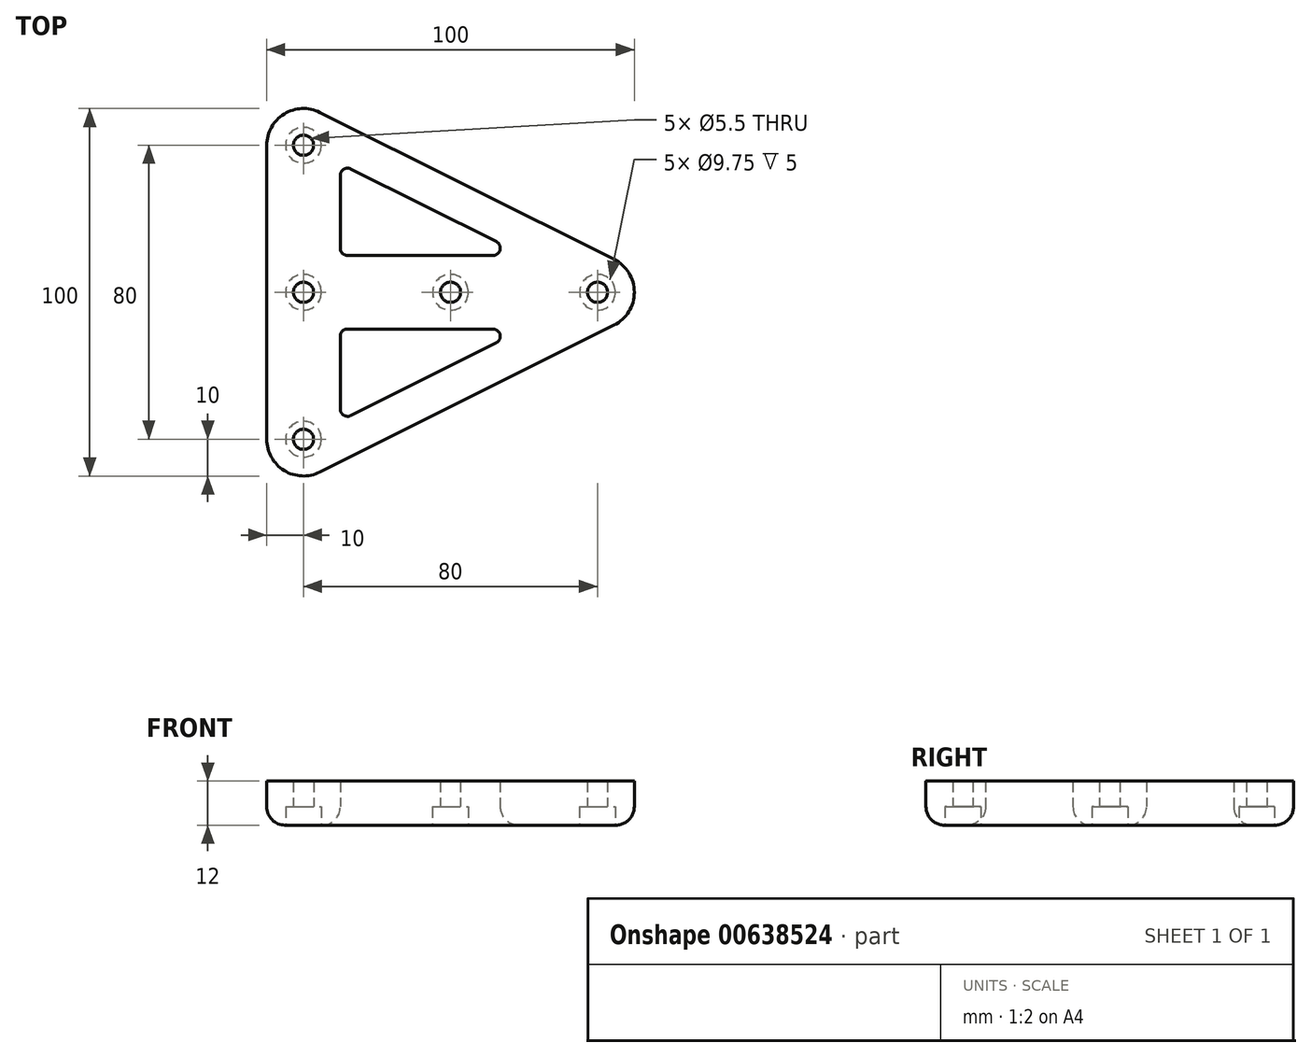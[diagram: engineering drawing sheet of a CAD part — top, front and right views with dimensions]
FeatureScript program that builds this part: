
annotation { "Feature Type Name" : "Feature", "Feature Type Description" : "" }
export const myFeature = defineFeature(function(context is Context, id is Id, definition is map)
    precondition{}
    {
        {
            var Q0;
            Q0=qCreatedBy(makeId("Top.planeOp"),FACE);
            var sketch = newSketch(context, id + "F0", { "sketchPlane" : qUnion([Q0])});
            skArc(sketch, "E0", {"start": v(4.47, 48.94) * mm, "mid": v(-5.26, 48.5) * mm, "end": v(-10, 40) * mm});
            skArc(sketch, "E1.MirrorC", {"start": v(4.47, -48.94) * mm, "mid": v(-5.26, -48.5) * mm, "end": v(-10, -40) * mm});
            skArc(sketch, "E2", {"start": v(84.47, -8.94) * mm, "mid": v(90, 0) * mm, "end": v(84.47, 8.94) * mm});
            skLineSegment(sketch, "E3", {"start": v(4.47, 48.94) * mm, "end": v(84.47, 8.94) * mm});
            skLineSegment(sketch, "E4", {"start": v(4.47, -48.94) * mm, "end": v(84.47, -8.94) * mm});
            skLineSegment(sketch, "E5", {"start": v(-10, 40) * mm, "end": v(-10, -40) * mm});
            skPoint(sketch, "E6", {"position": v(0, 0) * mm});
            skPoint(sketch, "E7", {"position": v(40, 0) * mm});
            skLineSegment(sketch, "E8.0", {"start": v(12.9, 33.55) * mm, "end": v(52.42, 13.79) * mm});
            skLineSegment(sketch, "E9.0", {"start": v(10, 31.76) * mm, "end": v(10, 12) * mm});
            skLineSegment(sketch, "E10.0", {"start": v(12, 10) * mm, "end": v(51.53, 10) * mm});
            skPoint(sketch, "E11.visualSharp", {"position": v(10, 35) * mm});
            skArc(sketch, "E11.filletArc", {"start": v(12.9, 33.55) * mm, "mid": v(10.95, 33.47) * mm, "end": v(10, 31.76) * mm});
            skPoint(sketch, "E12.visualSharp", {"position": v(10, 10) * mm});
            skArc(sketch, "E12.filletArc", {"start": v(10, 12) * mm, "mid": v(10.59, 10.59) * mm, "end": v(12, 10) * mm});
            skPoint(sketch, "E13.visualSharp", {"position": v(60, 10) * mm});
            skArc(sketch, "E13.filletArc", {"start": v(51.53, 10) * mm, "mid": v(53.47, 11.54) * mm, "end": v(52.42, 13.79) * mm});
            skArc(sketch, "E14.MirrorCS", {"start": v(10, -12) * mm, "mid": v(10.59, -10.59) * mm, "end": v(12, -10) * mm});
            skArc(sketch, "E15.MirrorCS", {"start": v(51.53, -10) * mm, "mid": v(53.47, -11.54) * mm, "end": v(52.42, -13.79) * mm});
            skPoint(sketch, "E16.MirrorP", {"position": v(10, -10) * mm});
            skArc(sketch, "E17.MirrorCS", {"start": v(12.9, -33.55) * mm, "mid": v(10.95, -33.47) * mm, "end": v(10, -31.76) * mm});
            skLineSegment(sketch, "E18.MirrorCS", {"start": v(10, -31.76) * mm, "end": v(10, -12) * mm});
            skLineSegment(sketch, "E19.MirrorCS", {"start": v(12, -10) * mm, "end": v(51.53, -10) * mm});
            skLineSegment(sketch, "E20.MirrorCS", {"start": v(12.9, -33.55) * mm, "end": v(52.42, -13.79) * mm});
            skSolve(sketch);
        }
        {
            var Q0;
            Q0=makeQuery(id+"F0.imprint","IMPRINT",FACE,{"disambiguationData":[TD([[makeQuery(id+"F0.imprint","IMPRINT",EDGE,{"derivedFrom":sQuery(id+"F0.wireOp",EDGE,"E0")}),1.0]])]});
            extrude(context, id + "F1", {"entities" : qUnion([Q0]), "depth" : 12 * mm, "offsetDistance" : 25 * mm});
        }
        {
            var Q0;
            Q0=sQuery(id+"F0.wireOp",VERTEX,"E0.center");
            var Q1;
            Q1=sQuery(id+"F0.wireOp",VERTEX,"E1.MirrorC.center");
            var Q2;
            Q2=sQuery(id+"F0.wireOp",VERTEX,"E6");
            var Q3;
            Q3=sQuery(id+"F0.wireOp",VERTEX,"E7");
            var Q4;
            Q4=sQuery(id+"F0.wireOp",VERTEX,"E2.center");
            var Q5;
            Q5=makeQuery(id+"F1.opExtrude","SWEPT_BODY",BODY,{"disambiguationData":[OSD([sQuery(id+"F0.wireOp",EDGE,"E0"),sQuery(id+"F0.wireOp",EDGE,"E1.MirrorC"),sQuery(id+"F0.wireOp",EDGE,"E2"),sQuery(id+"F0.wireOp",EDGE,"E3"),sQuery(id+"F0.wireOp",EDGE,"E4"),sQuery(id+"F0.wireOp",EDGE,"E5"),sQuery(id+"F0.wireOp",EDGE,"E8.0"),sQuery(id+"F0.wireOp",EDGE,"E9.0"),sQuery(id+"F0.wireOp",EDGE,"E10.0"),sQuery(id+"F0.wireOp",EDGE,"E11.filletArc"),sQuery(id+"F0.wireOp",EDGE,"E12.filletArc"),sQuery(id+"F0.wireOp",EDGE,"E13.filletArc"),sQuery(id+"F0.wireOp",EDGE,"E14.MirrorCS"),sQuery(id+"F0.wireOp",EDGE,"E15.MirrorCS"),sQuery(id+"F0.wireOp",EDGE,"E17.MirrorCS"),sQuery(id+"F0.wireOp",EDGE,"E18.MirrorCS"),sQuery(id+"F0.wireOp",EDGE,"E19.MirrorCS"),sQuery(id+"F0.wireOp",EDGE,"E20.MirrorCS")])]});
            hole(context, id + "F2", {"style" : HoleStyle.C_BORE, "endStyle" : HoleEndStyle.THROUGH, "oppositeDirection" : true, "standardTappedOrClearance" : lookupTablePath({ "standard" : "ISO", "fit" : "Normal", "size" : "M5", "type" : "Clearance" }), "standardBlindInLast" : lookupTablePath({ "fit" : "Standard", "standard" : "ISO", "size" : "M5", "type" : "Clearance" }), "holeDiameter" : 5.5 * mm, "cBoreDiameter" : 9.75 * mm, "cBoreDepth" : 5 * mm, "majorDiameter" : 5 * mm, "isTappedThrough" : true, "tappedDepth" : 12 * mm, "tapClearance" : 3, "locations" : qUnion([Q0, Q1, Q2, Q3, Q4]), "scope" : qUnion([Q5])});
        }
        {
            var Q0;
            Q0=makeQuery(id+"F1.opExtrude","CAP_EDGE",EDGE,{"disambiguationData":[OSD([sQuery(id+"F0.wireOp",EDGE,"E3")])],"isStart":true});
            var Q1;
            Q1=makeQuery(id+"F1.opExtrude","CAP_EDGE",EDGE,{"disambiguationData":[OSD([sQuery(id+"F0.wireOp",EDGE,"E8.0")])],"isStart":true});
            var Q2;
            Q2=makeQuery(id+"F1.opExtrude","CAP_EDGE",EDGE,{"disambiguationData":[OSD([sQuery(id+"F0.wireOp",EDGE,"E20.MirrorCS")])],"isStart":true});
            fillet(context, id + "F3", {"entities" : qUnion([Q0, Q1, Q2]), "radius" : 5 * mm, "tangentPropagation" : true, "allowEdgeOverflow" : false});
        }
    });
